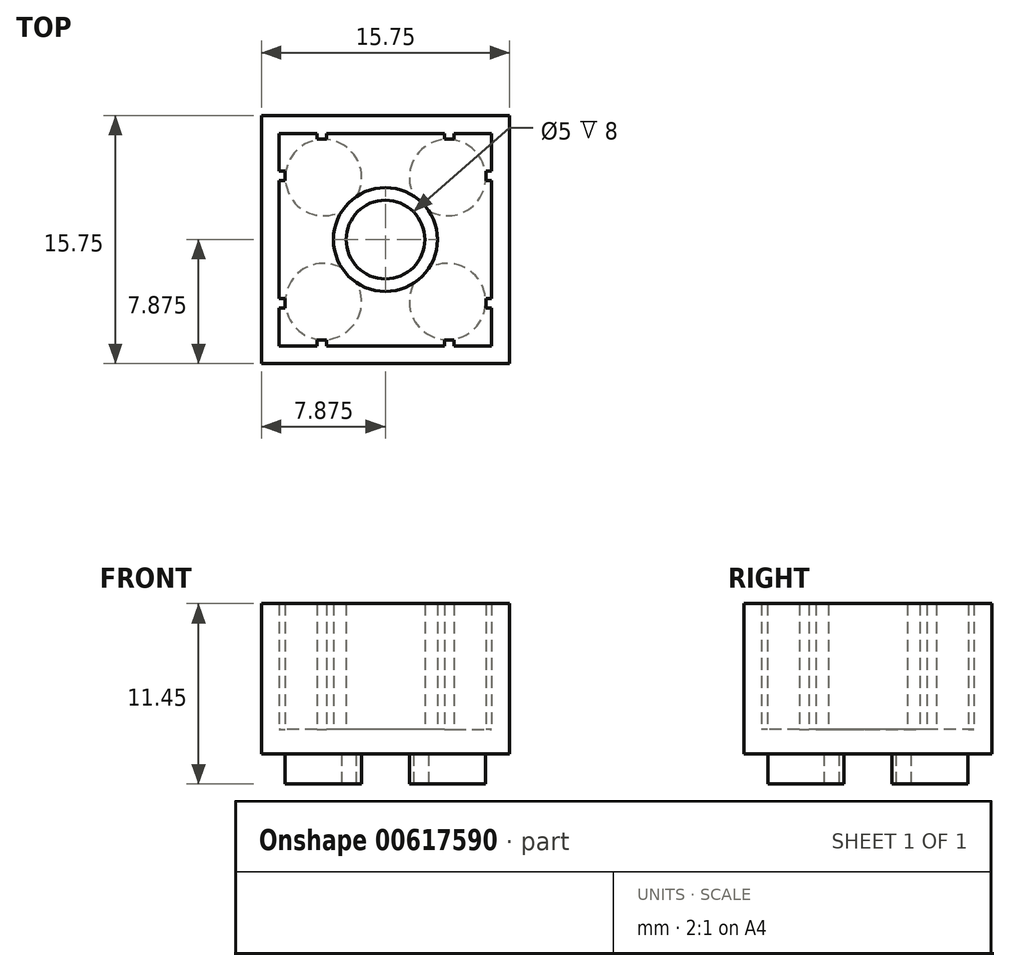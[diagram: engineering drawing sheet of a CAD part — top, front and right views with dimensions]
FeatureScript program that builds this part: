
annotation { "Feature Type Name" : "Feature", "Feature Type Description" : "" }
export const myFeature = defineFeature(function(context is Context, id is Id, definition is map)
    precondition{}
    {
        {
            var Q0;
            Q0=qCreatedBy(makeId("Top.planeOp"),FACE);
            var sketch = newSketch(context, id + "F0", { "sketchPlane" : qUnion([Q0])});
            skLineSegment(sketch, "E0", {"start": v(0, 0) * mm, "end": v(0, 15.75) * mm});
            skLineSegment(sketch, "E1", {"start": v(0, 15.75) * mm, "end": v(15.75, 15.75) * mm});
            skLineSegment(sketch, "E2", {"start": v(15.75, 15.75) * mm, "end": v(15.75, 0) * mm});
            skLineSegment(sketch, "E3", {"start": v(15.75, 0) * mm, "end": v(0, 0) * mm});
            skLineSegment(sketch, "E4.0", {"start": v(1.13, 14.62) * mm, "end": v(14.62, 14.62) * mm});
            skLineSegment(sketch, "E4.1", {"start": v(1.13, 1.13) * mm, "end": v(1.13, 14.62) * mm});
            skLineSegment(sketch, "E4.2", {"start": v(14.62, 1.13) * mm, "end": v(1.13, 1.13) * mm});
            skLineSegment(sketch, "E4.3", {"start": v(14.62, 14.62) * mm, "end": v(14.62, 1.13) * mm});
            skLineSegment(sketch, "E5", {"start": v(3.52, 14.62) * mm, "end": v(3.52, 14.25) * mm});
            skLineSegment(sketch, "E6", {"start": v(3.52, 14.25) * mm, "end": v(4.12, 14.25) * mm});
            skLineSegment(sketch, "E7", {"start": v(4.12, 14.25) * mm, "end": v(4.12, 14.62) * mm});
            skLineSegment(sketch, "E8", {"start": v(11.62, 14.62) * mm, "end": v(11.62, 14.25) * mm});
            skLineSegment(sketch, "E9", {"start": v(11.62, 14.25) * mm, "end": v(12.22, 14.25) * mm});
            skLineSegment(sketch, "E10", {"start": v(12.22, 14.25) * mm, "end": v(12.22, 14.62) * mm});
            skLineSegment(sketch, "E11", {"start": v(1.13, 12.22) * mm, "end": v(1.5, 12.22) * mm});
            skLineSegment(sketch, "E12", {"start": v(1.5, 12.22) * mm, "end": v(1.5, 11.62) * mm});
            skLineSegment(sketch, "E13", {"start": v(1.5, 11.62) * mm, "end": v(1.13, 11.62) * mm});
            skLineSegment(sketch, "E14", {"start": v(1.13, 3.52) * mm, "end": v(1.5, 3.52) * mm});
            skLineSegment(sketch, "E15", {"start": v(1.5, 3.52) * mm, "end": v(1.5, 4.12) * mm});
            skLineSegment(sketch, "E16", {"start": v(1.5, 4.12) * mm, "end": v(1.13, 4.12) * mm});
            skLineSegment(sketch, "E17", {"start": v(3.53, 1.13) * mm, "end": v(3.53, 1.5) * mm});
            skLineSegment(sketch, "E18", {"start": v(3.53, 1.5) * mm, "end": v(4.13, 1.5) * mm});
            skLineSegment(sketch, "E19", {"start": v(4.13, 1.5) * mm, "end": v(4.13, 1.13) * mm});
            skLineSegment(sketch, "E20", {"start": v(11.63, 1.13) * mm, "end": v(11.63, 1.5) * mm});
            skLineSegment(sketch, "E21", {"start": v(11.63, 1.5) * mm, "end": v(12.23, 1.5) * mm});
            skLineSegment(sketch, "E22", {"start": v(12.23, 1.5) * mm, "end": v(12.23, 1.13) * mm});
            skLineSegment(sketch, "E23", {"start": v(14.62, 12.23) * mm, "end": v(14.25, 12.23) * mm});
            skLineSegment(sketch, "E24", {"start": v(14.25, 12.23) * mm, "end": v(14.25, 11.63) * mm});
            skLineSegment(sketch, "E25", {"start": v(14.25, 11.63) * mm, "end": v(14.62, 11.63) * mm});
            skLineSegment(sketch, "E26", {"start": v(14.62, 3.52) * mm, "end": v(14.25, 3.52) * mm});
            skLineSegment(sketch, "E27", {"start": v(14.25, 3.52) * mm, "end": v(14.25, 4.12) * mm});
            skLineSegment(sketch, "E28", {"start": v(14.25, 4.12) * mm, "end": v(14.62, 4.12) * mm});
            skLineSegment(sketch, "E29", {"start": v(0, 7.88) * mm, "end": v(15.75, 7.88) * mm, "construction": true});
            skLineSegment(sketch, "E30", {"start": v(7.88, 15.75) * mm, "end": v(7.88, 0) * mm, "construction": true});
            skCircle(sketch, "E31", {"center": v(7.88, 7.88) * mm, "radius": 3.3 * mm});
            skCircle(sketch, "E32.0", {"center": v(7.88, 7.88) * mm, "radius": 2.5 * mm});
            skSolve(sketch);
        }
        {
            var Q0;
            Q0=makeQuery(id+"F0.imprint","IMPRINT",FACE,{"disambiguationData":[TD([[makeQuery(id+"F0.imprint","IMPRINT",EDGE,{"derivedFrom":sQuery(id+"F0.wireOp",EDGE,"E0")}),-1.0]])]});
            var Q1;
            {var subQ0=sQuery(id+"F0.wireOp",EDGE,"E5");Q1=makeQuery(id+"F0.imprint","IMPRINT",FACE,{"disambiguationData":[TD([[makeQuery(id+"F0.imprint","IMPRINT",EDGE,{"derivedFrom":subQ0}),1.0]])]});}
            var Q2;
            {var subQ0=sQuery(id+"F0.wireOp",EDGE,"E11");Q2=makeQuery(id+"F0.imprint","IMPRINT",FACE,{"disambiguationData":[TD([[makeQuery(id+"F0.imprint","IMPRINT",EDGE,{"derivedFrom":subQ0}),-1.0]])]});}
            var Q3;
            {var subQ0=sQuery(id+"F0.wireOp",EDGE,"E14");Q3=makeQuery(id+"F0.imprint","IMPRINT",FACE,{"disambiguationData":[TD([[makeQuery(id+"F0.imprint","IMPRINT",EDGE,{"derivedFrom":subQ0}),1.0]])]});}
            var Q4;
            {var subQ0=sQuery(id+"F0.wireOp",EDGE,"E17");Q4=makeQuery(id+"F0.imprint","IMPRINT",FACE,{"disambiguationData":[TD([[makeQuery(id+"F0.imprint","IMPRINT",EDGE,{"derivedFrom":subQ0}),-1.0]])]});}
            var Q5;
            {var subQ0=sQuery(id+"F0.wireOp",EDGE,"E20");Q5=makeQuery(id+"F0.imprint","IMPRINT",FACE,{"disambiguationData":[TD([[makeQuery(id+"F0.imprint","IMPRINT",EDGE,{"derivedFrom":subQ0}),-1.0]])]});}
            var Q6;
            {var subQ0=sQuery(id+"F0.wireOp",EDGE,"E26");Q6=makeQuery(id+"F0.imprint","IMPRINT",FACE,{"disambiguationData":[TD([[makeQuery(id+"F0.imprint","IMPRINT",EDGE,{"derivedFrom":subQ0}),-1.0]])]});}
            var Q7;
            {var subQ0=sQuery(id+"F0.wireOp",EDGE,"E23");Q7=makeQuery(id+"F0.imprint","IMPRINT",FACE,{"disambiguationData":[TD([[makeQuery(id+"F0.imprint","IMPRINT",EDGE,{"derivedFrom":subQ0}),1.0]])]});}
            var Q8;
            {var subQ0=sQuery(id+"F0.wireOp",EDGE,"E8");Q8=makeQuery(id+"F0.imprint","IMPRINT",FACE,{"disambiguationData":[TD([[makeQuery(id+"F0.imprint","IMPRINT",EDGE,{"derivedFrom":subQ0}),1.0]])]});}
            var Q9;
            Q9=makeQuery(id+"F0.imprint","IMPRINT",FACE,{"disambiguationData":[TD([[makeQuery(id+"F0.imprint","IMPRINT",EDGE,{"derivedFrom":sQuery(id+"F0.wireOp",EDGE,"E31")}),1.0]])]});
            extrude(context, id + "F1", {"entities" : qUnion([Q0, Q1, Q2, Q3, Q4, Q5, Q6, Q7, Q8, Q9]), "depth" : 9.55 * mm, "offsetDistance" : 25 * mm});
        }
        {
            var Q0;
            {var subQ3=sQuery(id+"F0.wireOp",EDGE,"E5");Q0=makeQuery(id+"F0.imprint","IMPRINT",FACE,{"disambiguationData":[TD([[makeQuery(id+"F0.imprint","IMPRINT",EDGE,{"derivedFrom":subQ3}),-1.0]])]});}
            var Q1;
            Q1=makeQuery(id+"F0.imprint","IMPRINT",FACE,{"disambiguationData":[TD([[makeQuery(id+"F0.imprint","IMPRINT",EDGE,{"derivedFrom":sQuery(id+"F0.wireOp",EDGE,"E32.0")}),1.0]])]});
            extrude(context, id + "F2", {"entities" : qUnion([Q0, Q1]), "operationType" : NewBodyOperationType.ADD, "depth" : 1.55 * mm, "offsetDistance" : 25 * mm});
        }
        {
            var Q0;
            {var subQ3=sQuery(id+"F0.wireOp",EDGE,"E5");Q0=makeQuery(id+"F0.imprint","IMPRINT",FACE,{"disambiguationData":[TD([[makeQuery(id+"F0.imprint","IMPRINT",EDGE,{"derivedFrom":subQ3}),-1.0]])]});}
            var sketch = newSketch(context, id + "F3", { "sketchPlane" : qUnion([Q0])});
            skLineSegment(sketch, "E33.bottom", {"start": v(0, 0) * mm, "end": v(15.75, 0) * mm});
            skLineSegment(sketch, "E33.top", {"start": v(0, 15.75) * mm, "end": v(15.75, 15.75) * mm});
            skLineSegment(sketch, "E33.left", {"start": v(0, 0) * mm, "end": v(0, 15.75) * mm});
            skLineSegment(sketch, "E33.right", {"start": v(15.75, 0) * mm, "end": v(15.75, 15.75) * mm});
            skLineSegment(sketch, "E34", {"start": v(7.88, 0) * mm, "end": v(7.88, 15.75) * mm, "construction": true});
            skLineSegment(sketch, "E35", {"start": v(0, 7.88) * mm, "end": v(15.75, 7.88) * mm, "construction": true});
            skLineSegment(sketch, "E36", {"start": v(7.88, 7.88) * mm, "end": v(0, 0) * mm, "construction": true});
            skLineSegment(sketch, "E37", {"start": v(7.88, 7.88) * mm, "end": v(15.75, 0) * mm, "construction": true});
            skLineSegment(sketch, "E38", {"start": v(7.88, 7.88) * mm, "end": v(15.75, 15.75) * mm, "construction": true});
            skLineSegment(sketch, "E39", {"start": v(7.88, 7.88) * mm, "end": v(0, 15.75) * mm, "construction": true});
            skCircle(sketch, "E40", {"center": v(3.94, 3.94) * mm, "radius": 2.43 * mm});
            skCircle(sketch, "E41", {"center": v(11.81, 3.94) * mm, "radius": 2.43 * mm});
            skCircle(sketch, "E42", {"center": v(11.81, 11.81) * mm, "radius": 2.43 * mm});
            skCircle(sketch, "E43", {"center": v(3.94, 11.81) * mm, "radius": 2.43 * mm});
            skSolve(sketch);
        }
        {
            var Q0;
            {var subQ0=sQuery(id+"F3.wireOp",EDGE,"E40");var subQ1=makeQuery(id+"F0.imprint","IMPRINT",EDGE,{"derivedFrom":sQuery(id+"F0.wireOp",EDGE,"E31")});var subQ2=makeQuery(id+"F3.imprint","INTERSECT",VERTEX,{"disambiguationData":[OD(0.0)],"derivedFrom":[subQ1,subQ0]});Q0=makeQuery(id+"F3.imprint","IMPRINT",FACE,{"disambiguationData":[TD([[makeQuery(id+"F3.imprint","IMPRINT",EDGE,{"disambiguationData":[TD([[subQ2,-1.0]])],"derivedFrom":subQ0}),1.0]])]});}
            var Q1;
            {var subQ0=sQuery(id+"F3.wireOp",EDGE,"E41");var subQ1=makeQuery(id+"F0.imprint","IMPRINT",EDGE,{"derivedFrom":sQuery(id+"F0.wireOp",EDGE,"E31")});var subQ2=makeQuery(id+"F3.imprint","INTERSECT",VERTEX,{"disambiguationData":[OD(0.0)],"derivedFrom":[subQ1,subQ0]});Q1=makeQuery(id+"F3.imprint","IMPRINT",FACE,{"disambiguationData":[TD([[makeQuery(id+"F3.imprint","IMPRINT",EDGE,{"disambiguationData":[TD([[subQ2,-1.0]])],"derivedFrom":subQ0}),1.0]])]});}
            var Q2;
            {var subQ0=sQuery(id+"F3.wireOp",EDGE,"E42");var subQ1=makeQuery(id+"F0.imprint","IMPRINT",EDGE,{"derivedFrom":sQuery(id+"F0.wireOp",EDGE,"E31")});var subQ2=makeQuery(id+"F3.imprint","INTERSECT",VERTEX,{"disambiguationData":[OD(0.0)],"derivedFrom":[subQ1,subQ0]});Q2=makeQuery(id+"F3.imprint","IMPRINT",FACE,{"disambiguationData":[TD([[makeQuery(id+"F3.imprint","IMPRINT",EDGE,{"disambiguationData":[TD([[subQ2,1.0]])],"derivedFrom":subQ0}),1.0]])]});}
            var Q3;
            {var subQ0=sQuery(id+"F3.wireOp",EDGE,"E43");var subQ1=makeQuery(id+"F0.imprint","IMPRINT",EDGE,{"derivedFrom":sQuery(id+"F0.wireOp",EDGE,"E31")});var subQ2=makeQuery(id+"F3.imprint","INTERSECT",VERTEX,{"disambiguationData":[OD(0.0)],"derivedFrom":[subQ1,subQ0]});Q3=makeQuery(id+"F3.imprint","IMPRINT",FACE,{"disambiguationData":[TD([[makeQuery(id+"F3.imprint","IMPRINT",EDGE,{"disambiguationData":[TD([[subQ2,1.0]])],"derivedFrom":subQ0}),1.0]])]});}
            extrude(context, id + "F4", {"entities" : qUnion([Q0, Q1, Q2, Q3]), "operationType" : NewBodyOperationType.ADD, "oppositeDirection" : true, "depth" : 1.9 * mm, "offsetDistance" : 25 * mm});
        }
    });
